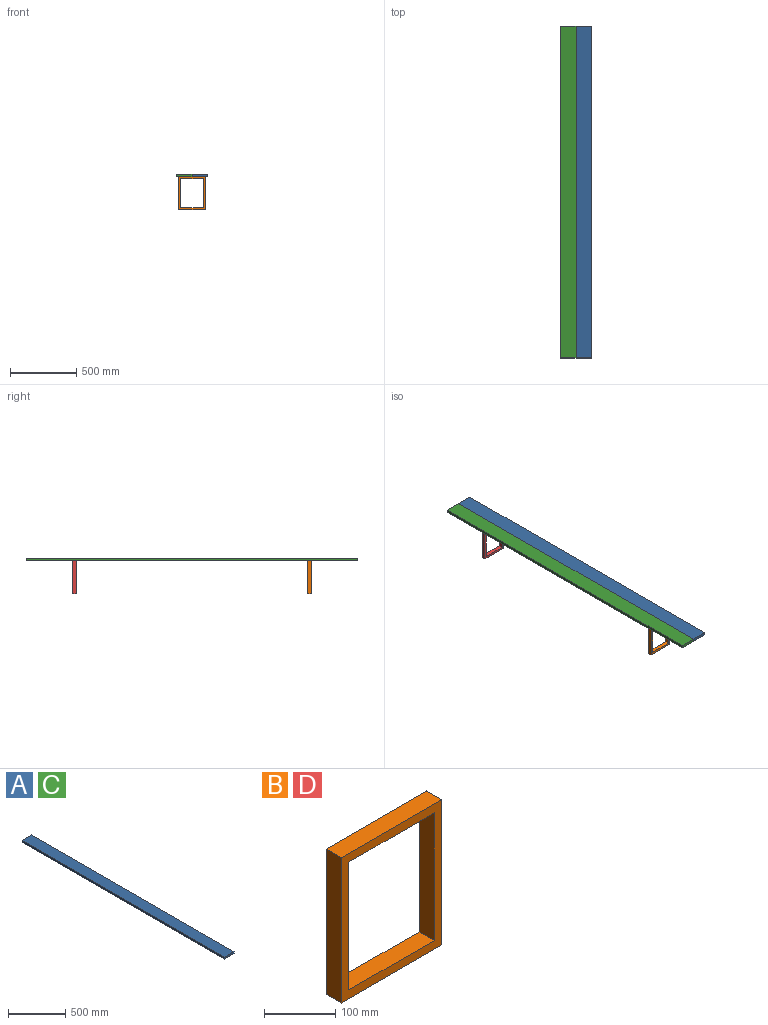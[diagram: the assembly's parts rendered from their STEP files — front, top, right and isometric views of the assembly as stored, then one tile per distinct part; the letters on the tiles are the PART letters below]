
ASSEMBLY  parts=4 mates=3
PART A: 6 faces, bbox 120x2500x20 mm
  f0: plane 2500x120mm, normal (0,0,1), area 300000mm2, adj f1,f3,f4,f5
  f1: plane 2500x20mm, normal (-1,0,0), area 50000mm2, adj f0,f2,f4,f5
  f2: plane 2500x120mm, normal (0,0,-1), area 300000mm2, adj f1,f3,f4,f5
  f3: plane 2500x20mm, normal (1,0,0), area 50000mm2, adj f0,f2,f4,f5
  f4: plane 120x20mm, normal (0,1,0), area 2400mm2, adj f0,f1,f2,f3
  f5: plane 120x20mm, normal (0,-1,0), area 2400mm2, adj f0,f1,f2,f3
PART B: 10 faces, bbox 200x30x250 mm
  f0: plane 200x30mm, normal (0,0,1), area 6000mm2, adj f1,f7,f8,f9
  f1: plane 250x30mm, normal (-1,0,0), area 7500mm2, adj f0,f2,f8,f9
  f2: plane 200x30mm, normal (0,0,-1), area 6000mm2, adj f1,f7,f8,f9
  f3: plane 220x30mm, normal (-1,0,0), area 6600mm2, adj f4,f6,f8,f9
  f4: plane 170x30mm, normal (0,0,1), area 5100mm2, adj f3,f5,f8,f9
  f5: plane 220x30mm, normal (1,0,0), area 6600mm2, adj f4,f6,f8,f9
  f6: plane 170x30mm, normal (0,0,-1), area 5100mm2, adj f3,f5,f8,f9
  f7: plane 250x30mm, normal (1,0,0), area 7500mm2, adj f0,f2,f8,f9
  f8: plane 250x200mm, normal (0,1,0), area 12600mm2, adj f0,f1,f2,f3,f4,f5,f6,f7
  f9: plane 250x200mm, normal (0,-1,0), area 12600mm2, adj f0,f1,f2,f3,f4,f5,f6,f7
PART C: same geometry as A
PART D: same geometry as B
PLACE A t=(936.06,-1070.65,-222.3)mm
PLACE B t=(1091.13,-720.65,-331.3)mm
PLACE C t=(816.06,-1070.65,-222.3)mm
PLACE D t=(1091.13,1049.35,-331.3)mm
MATE fastened B.f0 <-> C.f2  axis (0,0,1) through (512.34,-720.65,-323.24)mm
MATE fastened D.f0 <-> C.f2  axis (0,0,1) through (512.34,1079.35,-323.24)mm
MATE fastened C.f3 <-> A.f1  axis (1,0,0) through (612.34,-1070.65,-303.24)mm
